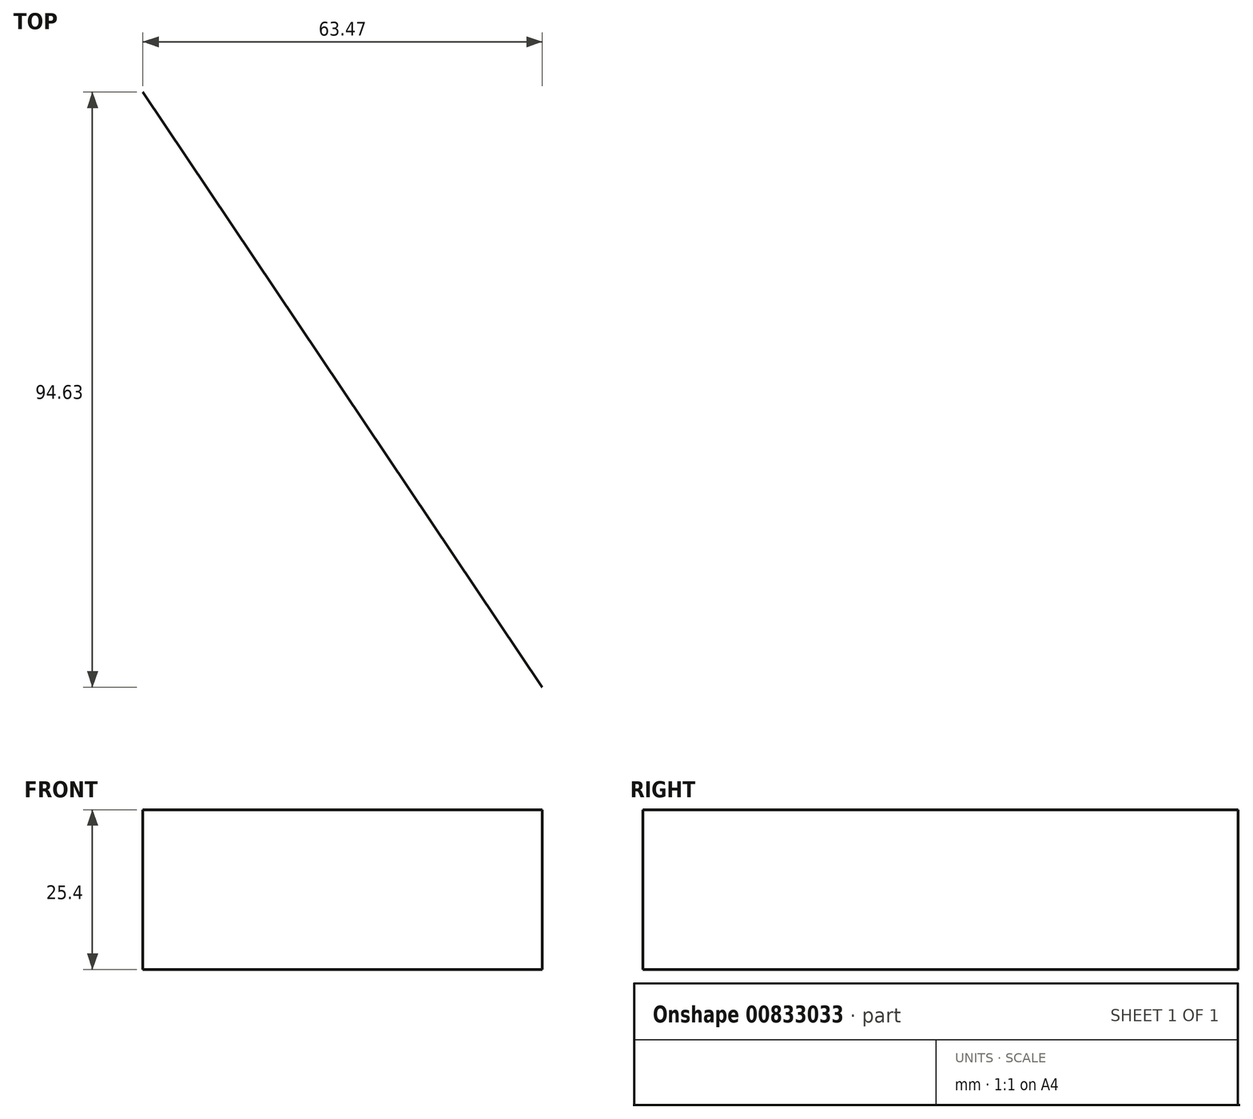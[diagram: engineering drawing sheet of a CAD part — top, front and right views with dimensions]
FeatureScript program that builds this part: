
annotation { "Feature Type Name" : "Feature", "Feature Type Description" : "" }
export const myFeature = defineFeature(function(context is Context, id is Id, definition is map)
    precondition{}
    {
        {
            var Q0;
            Q0=qCreatedBy(makeId("Top.planeOp"),FACE);
            var sketch = newSketch(context, id + "F0", { "sketchPlane" : qUnion([Q0])});
            skLineSegment(sketch, "E0", {"start": v(-63.47, 94.63) * mm, "end": v(0, 0) * mm});
            skLineSegment(sketch, "E1", {"start": v(0, 0) * mm, "end": v(15.66, 28.4) * mm});
            skLineSegment(sketch, "E2", {"start": v(15.66, 28.4) * mm, "end": v(-3.27, 72.74) * mm});
            skLineSegment(sketch, "E3", {"start": v(-3.27, 72.74) * mm, "end": v(79.6, -51.53) * mm});
            skSolve(sketch);
        }
        {
            var Q0;
            Q0=sQuery(id+"F0.wireOp",EDGE,"E0");
            extrude(context, id + "F1", {"bodyType" : ToolBodyType.SURFACE, "surfaceEntities" : qUnion([Q0]), "depth" : 25.4 * mm, "offsetDistance" : 25.4 * mm});
        }
    });
